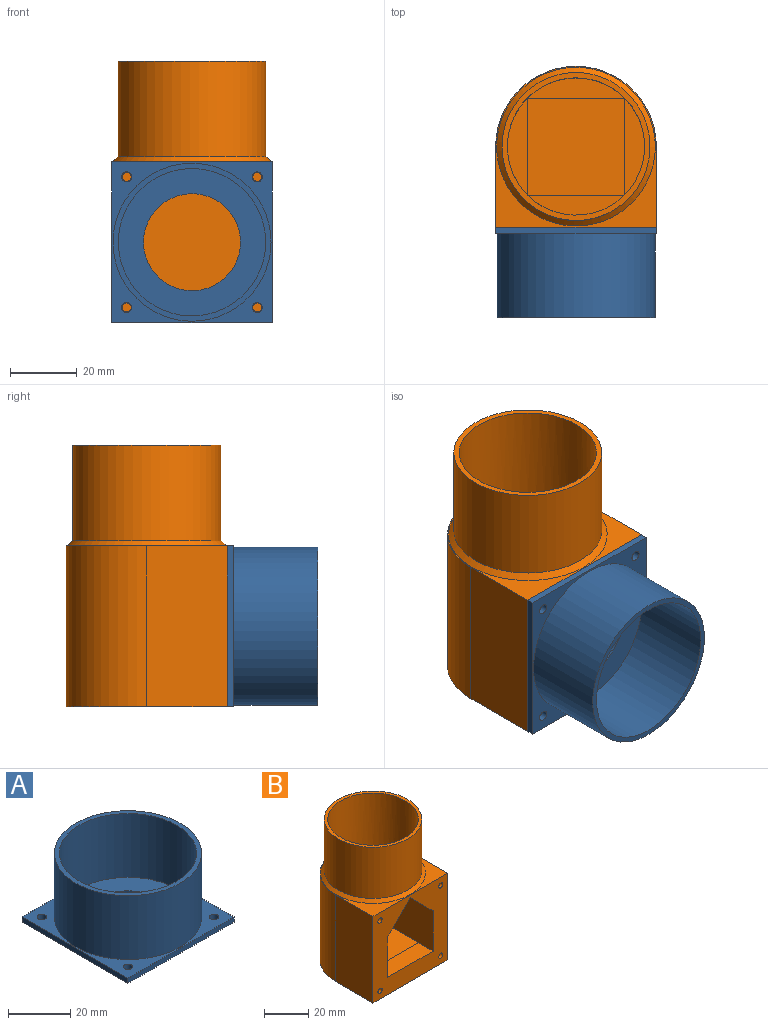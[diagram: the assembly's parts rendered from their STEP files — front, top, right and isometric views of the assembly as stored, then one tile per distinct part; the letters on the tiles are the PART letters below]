
ASSEMBLY  parts=2 mates=1
PART A: 15 faces, bbox 48x48x27 mm
  f0: plane 44x44mm, normal (0,0,1), area 860mm2, adj f7,f12
  f1: plane 48x2mm, normal (1,0,0), area 96mm2, adj f2,f8,f10,f11
  f2: plane 48x2mm, normal (0,1,0), area 96mm2, adj f1,f3,f10,f11
  f3: plane 48x2mm, normal (-1,0,0), area 96mm2, adj f2,f8,f10,f11
  f4: cylinder r=1.5mm len=3mm, axis (0,0,-1), area 18.8mm2, adj f10,f11
  f5: cylinder r=1.5mm len=3mm, axis (0,0,-1), area 18.8mm2, adj f10,f11
  f6: cylinder r=1.5mm len=3mm, axis (0,0,-1), area 18.8mm2, adj f10,f11
  f7: cylinder r=14.5mm len=29mm, axis (0,0,-1), area 182.2mm2, adj f0,f11
  f8: plane 48x2mm, normal (0,-1,0), area 96mm2, adj f1,f3,f10,f11
  f9: cylinder r=1.5mm len=3mm, axis (0,0,-1), area 18.8mm2, adj f10,f11
  f10: plane 48x48mm, normal (0,0,1), area 526mm2, adj f1,f2,f3,f4,f5,f6,f8,f9
  f11: plane 48x48mm, normal (0,0,-1), area 1615.2mm2, adj f1,f2,f3,f4,f5,f6,f7,f8
  f12: cylinder r=22mm len=44mm, axis (0,0,-1), area 3455.8mm2, adj f0,f14
  f13: cylinder r=23.6mm len=47.2mm, axis (0,0,-1), area 3707.1mm2, adj f10,f14
  f14: plane 47.2x47.2mm, normal (0,0,1), area 229.2mm2, adj f12,f13
PART B: 30 faces, bbox 48x48x78 mm
  f0: plane 48x48mm, normal (0,-1,0), area 1421.6mm2, adj f4,f6,f7,f8,f14,f16,f18,f19
  f1: plane 28.99x6mm, normal (0,0,1), area 119.9mm2, adj f9,f13
  f2: plane 28.99x6mm, normal (0,0,1), area 119.9mm2, adj f9,f14
  f3: plane 28.99x6mm, normal (0,0,1), area 119.9mm2, adj f9,f15
  f4: plane 48x24mm, normal (1,0,0), area 1152mm2, adj f0,f5,f7,f8
  f5: cylinder r=24mm len=48mm, axis (0,0,-1), area 3619.1mm2, adj f4,f6,f7,f8
  f6: plane 48x24mm, normal (-1,0,0), area 1152mm2, adj f0,f5,f7,f8
  f7: plane 48x48mm, normal (0,0,1), area 292.2mm2, adj f0,f4,f5,f6,f29
  f8: plane 48x48mm, normal (0,0,-1), area 2056.8mm2, adj f0,f4,f5,f6
  f9: cylinder r=20.5mm len=41mm, axis (0,0,-1), area 3864.2mm2, adj f1,f2,f3,f11,f12
  f10: cylinder r=22.1mm len=44.2mm, axis (0,0,-1), area 3943.6mm2, adj f11,f29
  f11: plane 44.2x44.2mm, normal (0,0,1), area 214.1mm2, adj f9,f10
  f12: plane 28.99x6mm, normal (0,0,1), area 119.9mm2, adj f9,f16
  f13: plane 28.99x16.1mm, normal (0,1,0), area 256.5mm2, adj f1,f14,f16,f19,f20
  f14: plane 38.5x38.5mm, normal (-1,0,0), area 1329.1mm2, adj f0,f2,f13,f15,f17,f18,f20
  f15: plane 38.5x28.99mm, normal (0,-1,0), area 1116.2mm2, adj f3,f14,f16,f17
  f16: plane 38.5x38.5mm, normal (1,0,0), area 1329.1mm2, adj f0,f12,f13,f15,f17,f18,f19
  f17: plane 29x29mm, normal (0,0,1), area 840.5mm2, adj f14,f15,f16,f18
  f18: plane 29x9.51mm, normal (0,0,1), area 275.5mm2, adj f0,f14,f16,f17
  f19: plane 14.5x14.5mm, normal (0.71,0,-0.71), area 194.8mm2, adj f0,f13,f16,f20
  f20: plane 14.5x14.5mm, normal (-0.71,0,-0.71), area 194.8mm2, adj f0,f13,f14,f19
  f21: cylinder r=1.35mm len=25mm, axis (0,-1,0), area 212.1mm2, adj f0,f22
  f22: plane 2.7x2.7mm, normal (0,-1,0), area 5.7mm2, adj f21
  f23: cylinder r=1.35mm len=25mm, axis (0,-1,0), area 212.1mm2, adj f0,f24
  f24: plane 2.7x2.7mm, normal (0,-1,0), area 5.7mm2, adj f23
  f25: cylinder r=1.35mm len=25mm, axis (0,-1,0), area 212.1mm2, adj f0,f26
  f26: plane 2.7x2.7mm, normal (0,-1,0), area 5.7mm2, adj f25
  f27: cylinder r=1.35mm len=25mm, axis (0,-1,0), area 212.1mm2, adj f0,f28
  f28: plane 2.7x2.7mm, normal (0,-1,0), area 5.7mm2, adj f27
  f29: cone r=22.1mm half-angle=45deg, axis (0,0,-1), area 325.6mm2, adj f7,f10
PLACE A rot(axis=(1,0,0),90deg) t=(0,-34.6,13.5)mm
PLACE B t=(0,-10.6,-10.5)mm
MATE fastened B.f23 <-> A.f6  axis (0,-1,0) through (19.5,-34.6,33)mm
